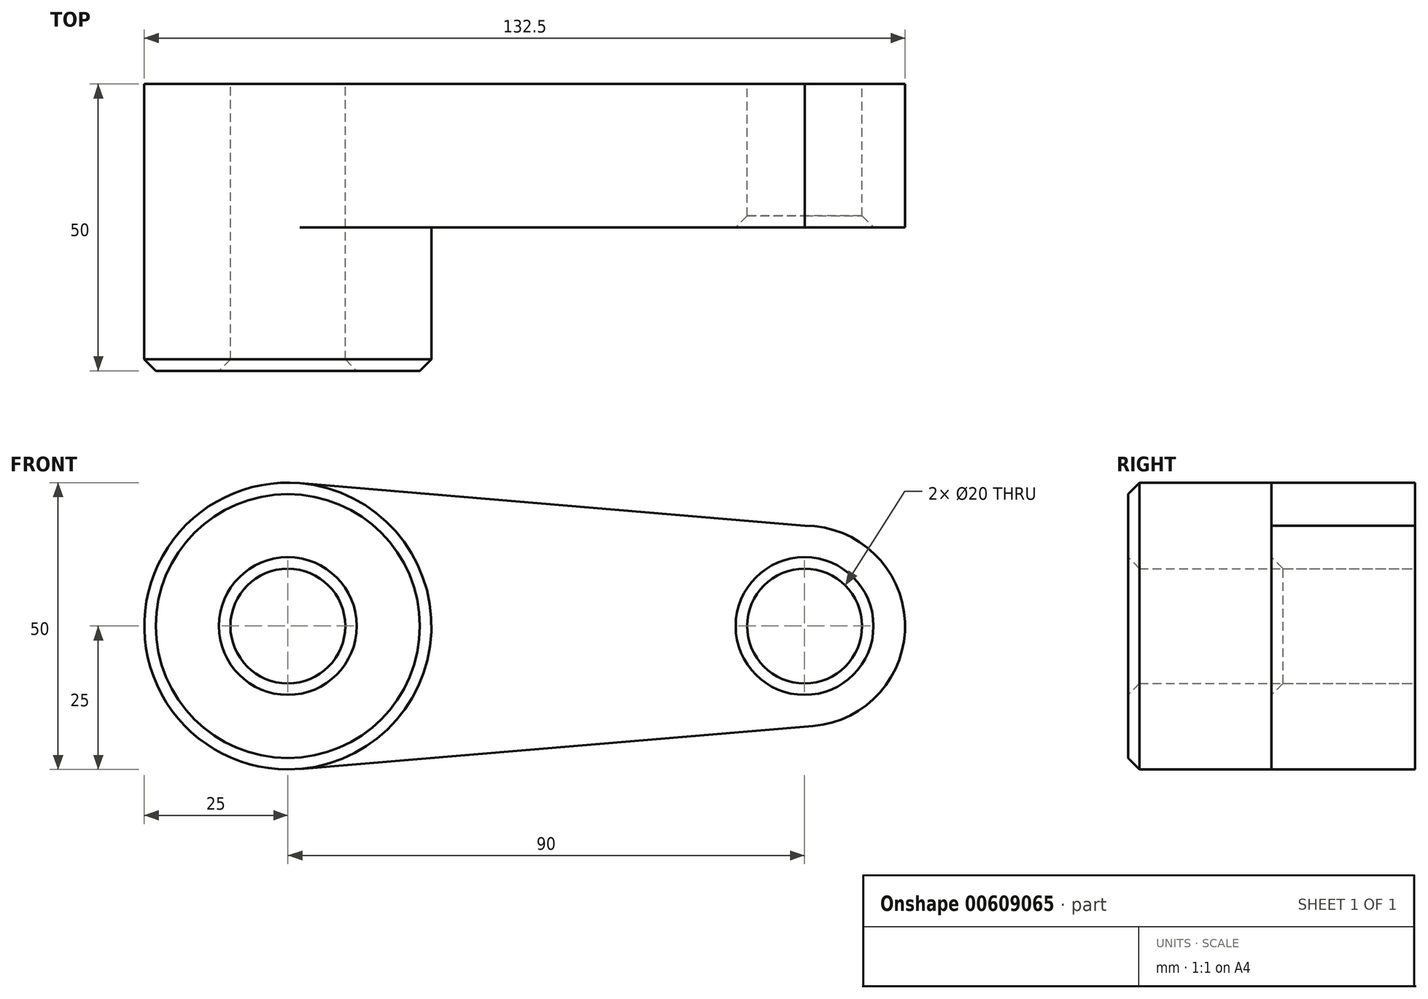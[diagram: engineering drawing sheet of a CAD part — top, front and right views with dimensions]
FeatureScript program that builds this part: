
annotation { "Feature Type Name" : "Feature", "Feature Type Description" : "" }
export const myFeature = defineFeature(function(context is Context, id is Id, definition is map)
    precondition{}
    {
        {
            var Q0;
            Q0=qCreatedBy(makeId("Front.planeOp"),FACE);
            var sketch = newSketch(context, id + "F0", { "sketchPlane" : qUnion([Q0])});
            skCircle(sketch, "E0", {"center": v(0, 0) * mm, "radius": 25 * mm});
            skCircle(sketch, "E1", {"center": v(90, 0) * mm, "radius": 17.5 * mm});
            skLineSegment(sketch, "E2", {"start": v(90.02, 17.5) * mm, "end": v(0, 25.09) * mm});
            skLineSegment(sketch, "E3", {"start": v(2.08, -24.91) * mm, "end": v(91.46, -17.44) * mm});
            skCircle(sketch, "E4", {"center": v(0, 0) * mm, "radius": 10 * mm});
            skCircle(sketch, "E5", {"center": v(90, 0) * mm, "radius": 10 * mm});
            skSolve(sketch);
        }
        {
            var Q0;
            Q0 = qSketchRegion(id + "F0", true);
            extrude(context, id + "F1", {"entities" : qUnion([Q0]), "depth" : 25 * mm, "offsetDistance" : 25.4 * mm});
        }
        {
            var Q0;
            Q0=makeQuery(id+"F0.imprint","IMPRINT",FACE,{"disambiguationData":[TD([[makeQuery(id+"F0.imprint","IMPRINT",EDGE,{"derivedFrom":sQuery(id+"F0.wireOp",EDGE,"E4")}),-1.0]])]});
            var sketch = newSketch(context, id + "F2", { "sketchPlane" : qUnion([Q0])});
            skSolve(sketch);
        }
        {
            var Q0;
            Q0=makeQuery(id+"F2.imprint","IMPRINT",FACE,{"disambiguationData":[TD([[makeQuery(id+"F2.imprint","IMPRINT",EDGE,{"derivedFrom":makeQuery(id+"F0.imprint","IMPRINT",EDGE,{"derivedFrom":sQuery(id+"F0.wireOp",EDGE,"E4")})}),-1.0]])]});
            extrude(context, id + "F3", {"entities" : qUnion([Q0]), "operationType" : NewBodyOperationType.ADD, "depth" : 50 * mm, "offsetDistance" : 25.4 * mm});
        }
        {
            var Q0;
            Q0=makeQuery(id+"F3.opExtrude","CAP_EDGE",EDGE,{"disambiguationData":[OSD([sQuery(id+"F0.wireOp",EDGE,"E0")])],"isStart":false});
            var Q1;
            Q1=makeQuery(id+"F3.opExtrude","CAP_EDGE",EDGE,{"disambiguationData":[OSD([sQuery(id+"F0.wireOp",EDGE,"E4")])],"isStart":false});
            var Q2;
            Q2=makeQuery(id+"F1.opExtrude","CAP_EDGE",EDGE,{"disambiguationData":[OSD([sQuery(id+"F0.wireOp",EDGE,"E5")])],"isStart":false});
            chamfer(context, id + "F4", {"entities" : qUnion([Q0, Q1, Q2]), "width" : 2 * mm, "tangentPropagation" : true});
        }
    });
